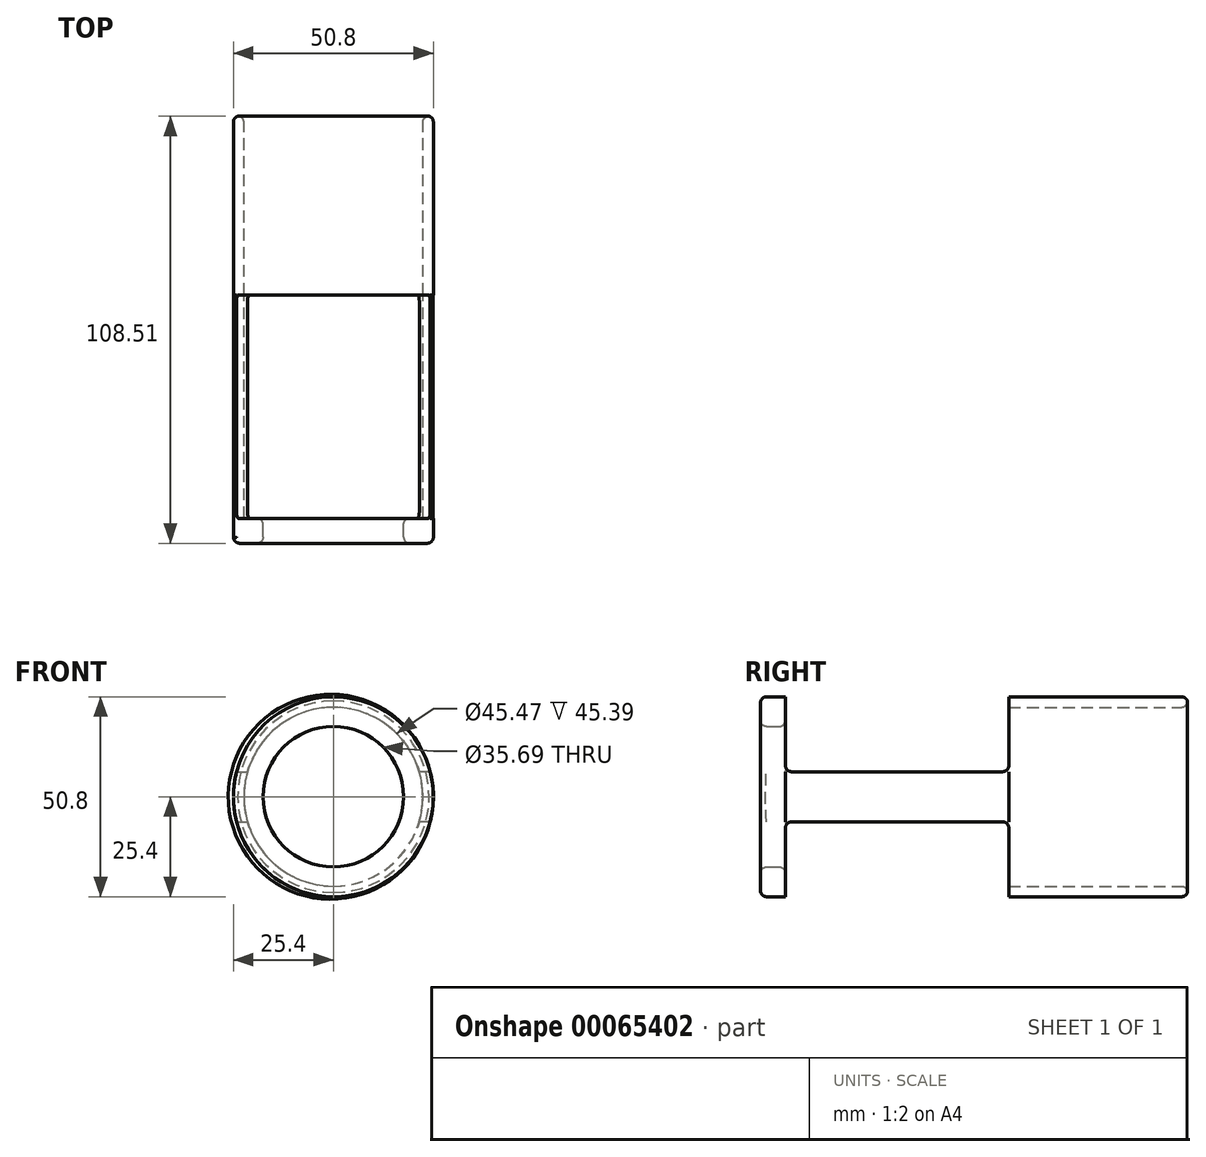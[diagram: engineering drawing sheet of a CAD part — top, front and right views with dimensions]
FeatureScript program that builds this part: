
annotation { "Feature Type Name" : "Feature", "Feature Type Description" : "" }
export const myFeature = defineFeature(function(context is Context, id is Id, definition is map)
    precondition{}
    {
        {
            var Q0;
            Q0=qCreatedBy(makeId("Front.planeOp"),FACE);
            var sketch = newSketch(context, id + "F0", { "sketchPlane" : qUnion([Q0])});
            skCircle(sketch, "E0", {"center": v(0, 0) * mm, "radius": 25.4 * mm});
            skCircle(sketch, "E1", {"center": v(0, 0) * mm, "radius": 22.73 * mm});
            skSolve(sketch);
        }
        {
            var Q0;
            Q0=makeQuery(id+"F0.imprint","IMPRINT",FACE,{"disambiguationData":[TD([[makeQuery(id+"F0.imprint","IMPRINT",EDGE,{"derivedFrom":sQuery(id+"F0.wireOp",EDGE,"E0")}),1.0]])]});
            extrude(context, id + "F1", {"entities" : qUnion([Q0]), "depth" : 45.4 * mm});
        }
        {
            var Q0;
            Q0=makeQuery(id+"F1.opExtrude","CAP_FACE",FACE,{"disambiguationData":[OSD([sQuery(id+"F0.wireOp",EDGE,"E0"),sQuery(id+"F0.wireOp",EDGE,"E1")])],"isStart":false});
            var sketch = newSketch(context, id + "F2", { "sketchPlane" : qUnion([Q0])});
            skLineSegment(sketch, "E2", {"start": v(-24.6, -6.36) * mm, "end": v(-21.83, -6.36) * mm});
            skLineSegment(sketch, "E3", {"start": v(-24.6, 6.36) * mm, "end": v(-21.83, 6.36) * mm});
            skArc(sketch, "E4", {"start": v(-21.83, 6.36) * mm, "mid": v(-22.72, 0) * mm, "end": v(-21.83, -6.36) * mm});
            skArc(sketch, "E5", {"start": v(-24.6, 6.36) * mm, "mid": v(-25.38, 0) * mm, "end": v(-24.6, -6.36) * mm});
            skPoint(sketch, "E6.start.orphan", {"position": v(-31.11, 0) * mm});
            skSolve(sketch);
        }
        {
            var Q0;
            {var subQ0=sQuery(id+"F2.wireOp",EDGE,"E4");Q0=makeQuery(id+"F2.imprint","IMPRINT",FACE,{"disambiguationData":[TD([[makeQuery(id+"F2.imprint","IMPRINT",EDGE,{"derivedFrom":subQ0}),-1.0]])]});}
            var Q1;
            {var subQ0=sQuery(id+"F2.wireOp",EDGE,"E2");Q1=makeQuery(id+"F2.imprint","IMPRINT",FACE,{"disambiguationData":[TD([[makeQuery(id+"F2.imprint","IMPRINT",EDGE,{"derivedFrom":subQ0}),1.0]])]});}
            extrude(context, id + "F3", {"entities" : qUnion([Q0, Q1]), "operationType" : NewBodyOperationType.ADD, "depth" : 56.77 * mm});
        }
        {
            var Q0;
            Q0=makeQuery(id+"F1.opExtrude","SWEPT_BODY",BODY,{"disambiguationData":[OSD([sQuery(id+"F0.wireOp",EDGE,"E0"),sQuery(id+"F0.wireOp",EDGE,"E1")])]});
            var Q1;
            Q1=qCreatedBy(makeId("Right.planeOp"),FACE);
            mirror(context, id + "F4", {"operationType" : NewBodyOperationType.ADD, "entities" : qUnion([Q0]), "mirrorPlane" : qUnion([Q1])});
        }
        {
            var Q0;
            Q0=makeQuery(id+"F3.opExtrude","CAP_FACE",FACE,{"disambiguationData":[OSD([sQuery(id+"F2.wireOp",EDGE,"E2"),sQuery(id+"F2.wireOp",EDGE,"E3"),sQuery(id+"F2.wireOp",EDGE,"E4"),sQuery(id+"F2.wireOp",EDGE,"E5")])],"isStart":false});
            var sketch = newSketch(context, id + "F5", { "sketchPlane" : qUnion([Q0])});
            skCircle(sketch, "E7", {"center": v(0, 0) * mm, "radius": 25.4 * mm});
            skCircle(sketch, "E8", {"center": v(0, 0) * mm, "radius": 17.84 * mm});
            skSolve(sketch);
        }
        {
            var Q0;
            Q0=makeQuery(id+"F5.imprint","IMPRINT",FACE,{"disambiguationData":[TD([[makeQuery(id+"F5.imprint","IMPRINT",EDGE,{"derivedFrom":makeQuery(id+"F3.opExtrude","CAP_EDGE",EDGE,{"disambiguationData":[OSD([sQuery(id+"F2.wireOp",EDGE,"E2")])],"isStart":false})}),1.0]])]});
            var Q1;
            Q1=makeQuery(id+"F5.imprint","IMPRINT",FACE,{"disambiguationData":[TD([[makeQuery(id+"F5.imprint","IMPRINT",EDGE,{"derivedFrom":sQuery(id+"F5.wireOp",EDGE,"E8")}),-1.0]])]});
            extrude(context, id + "F6", {"entities" : qUnion([Q0, Q1]), "operationType" : NewBodyOperationType.ADD, "depth" : 6.35 * mm});
        }
        {
            var Q0;
            Q0=makeQuery(id+"F3.opExtrude","CAP_EDGE",EDGE,{"disambiguationData":[OSD([sQuery(id+"F2.wireOp",EDGE,"E2")])],"isStart":true});
            var Q1;
            Q1=makeQuery(id+"F4.opPattern","COPY",EDGE,{"derivedFrom":makeQuery(id+"F3.opExtrude","CAP_EDGE",EDGE,{"disambiguationData":[OSD([sQuery(id+"F2.wireOp",EDGE,"E2")])],"isStart":true}),"instanceName":"1"});
            var Q2;
            Q2=makeQuery(id+"F3.opExtrude","CAP_EDGE",EDGE,{"disambiguationData":[OSD([sQuery(id+"F2.wireOp",EDGE,"E3")])],"isStart":true});
            var Q3;
            Q3=makeQuery(id+"F4.opPattern","COPY",EDGE,{"derivedFrom":makeQuery(id+"F3.opExtrude","CAP_EDGE",EDGE,{"disambiguationData":[OSD([sQuery(id+"F2.wireOp",EDGE,"E3")])],"isStart":true}),"instanceName":"1"});
            var Q4;
            Q4=makeQuery(id+"F3.opExtrude","CAP_EDGE",EDGE,{"disambiguationData":[OSD([sQuery(id+"F2.wireOp",EDGE,"E3")])],"isStart":false});
            var Q5;
            Q5=makeQuery(id+"F4.opPattern","COPY",EDGE,{"derivedFrom":makeQuery(id+"F3.opExtrude","CAP_EDGE",EDGE,{"disambiguationData":[OSD([sQuery(id+"F2.wireOp",EDGE,"E3")])],"isStart":false}),"instanceName":"1"});
            var Q6;
            Q6=makeQuery(id+"F3.opExtrude","CAP_EDGE",EDGE,{"disambiguationData":[OSD([sQuery(id+"F2.wireOp",EDGE,"E2")])],"isStart":false});
            var Q7;
            Q7=makeQuery(id+"F4.opPattern","COPY",EDGE,{"derivedFrom":makeQuery(id+"F3.opExtrude","CAP_EDGE",EDGE,{"disambiguationData":[OSD([sQuery(id+"F2.wireOp",EDGE,"E2")])],"isStart":false}),"instanceName":"1"});
            var Q8;
            Q8=makeQuery(id+"F1.opExtrude","CAP_EDGE",EDGE,{"disambiguationData":[OSD([sQuery(id+"F0.wireOp",EDGE,"E1")])],"isStart":true});
            fillet(context, id + "F7", {"entities" : qUnion([Q0, Q1, Q2, Q3, Q4, Q5, Q6, Q7, Q8]), "radius" : 1.59 * mm, "tangentPropagation" : true, "allowEdgeOverflow" : false});
        }
        {
            var Q0;
            Q0=makeQuery(id+"F6.opExtrude","CAP_EDGE",EDGE,{"disambiguationData":[OSD([sQuery(id+"F5.wireOp",EDGE,"E8")])],"isStart":false});
            var Q1;
            Q1=makeQuery(id+"F6.opExtrude","CAP_EDGE",EDGE,{"disambiguationData":[OSD([sQuery(id+"F5.wireOp",EDGE,"E8")])],"isStart":true});
            var Q2;
            Q2=makeQuery(id+"F6.opExtrude","CAP_EDGE",EDGE,{"disambiguationData":[OSD([sQuery(id+"F5.wireOp",EDGE,"E7")])],"isStart":false});
            var Q3;
            Q3=makeQuery(id+"F1.opExtrude","CAP_EDGE",EDGE,{"disambiguationData":[OSD([sQuery(id+"F0.wireOp",EDGE,"E0")])],"isStart":true});
            fillet(context, id + "F8", {"entities" : qUnion([Q0, Q1, Q2, Q3]), "radius" : 1.59 * mm, "tangentPropagation" : true, "allowEdgeOverflow" : false});
        }
    });
